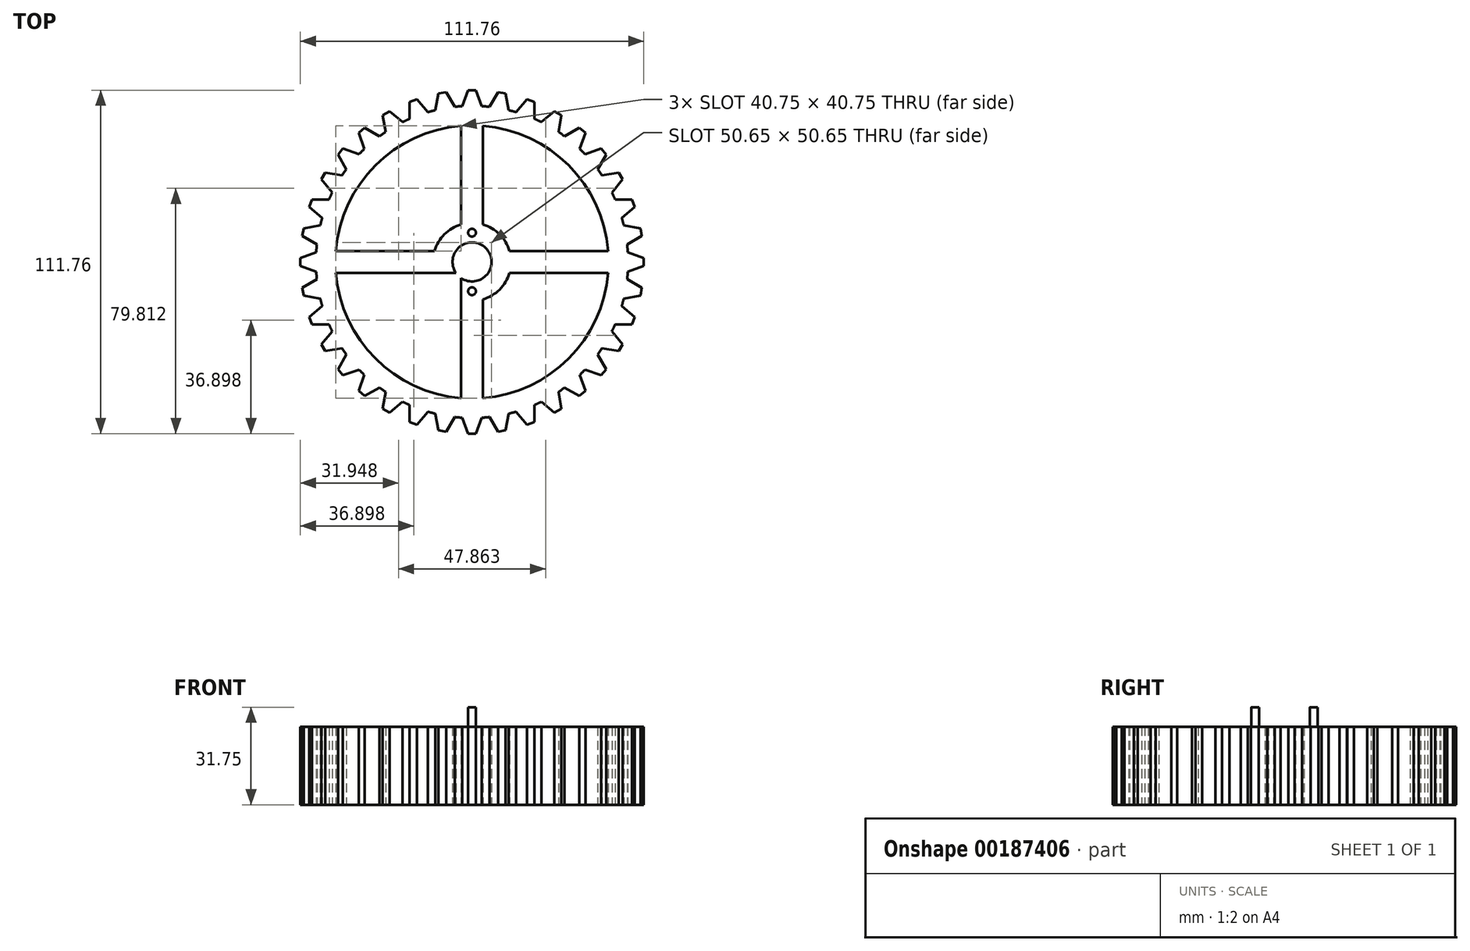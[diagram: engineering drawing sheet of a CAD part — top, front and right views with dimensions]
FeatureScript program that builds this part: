
annotation { "Feature Type Name" : "Feature", "Feature Type Description" : "" }
export const myFeature = defineFeature(function(context is Context, id is Id, definition is map)
    precondition{}
    {
        {
            var Q0;
            Q0=qCreatedBy(makeId("Top.planeOp"),FACE);
            var sketch = newSketch(context, id + "F0", { "sketchPlane" : qUnion([Q0])});
            skCircle(sketch, "E0", {"center": v(0, 0) * mm, "radius": 50.8 * mm});
            skLineSegment(sketch, "E1", {"start": v(0, 49.78) * mm, "end": v(3.56, 49.78) * mm});
            skLineSegment(sketch, "E2", {"start": v(0, 49.78) * mm, "end": v(-3.56, 49.78) * mm});
            skLineSegment(sketch, "E3", {"start": v(0, 55.88) * mm, "end": v(-1.27, 55.88) * mm});
            skLineSegment(sketch, "E4", {"start": v(0, 55.88) * mm, "end": v(1.27, 55.88) * mm});
            skLineSegment(sketch, "E5", {"start": v(-1.27, 55.88) * mm, "end": v(-3.56, 49.78) * mm});
            skLineSegment(sketch, "E6", {"start": v(1.27, 55.88) * mm, "end": v(3.56, 49.78) * mm});
            skLineSegment(sketch, "E7.1.0", {"start": v(10.95, 54.81) * mm, "end": v(12.15, 48.41) * mm});
            skLineSegment(sketch, "E7.1.1", {"start": v(9.7, 55.03) * mm, "end": v(10.95, 54.81) * mm});
            skLineSegment(sketch, "E7.1.2", {"start": v(9.7, 55.03) * mm, "end": v(8.45, 55.25) * mm});
            skLineSegment(sketch, "E7.1.3", {"start": v(8.45, 55.25) * mm, "end": v(5.14, 49.65) * mm});
            skLineSegment(sketch, "E7.1.4", {"start": v(8.64, 49.03) * mm, "end": v(5.14, 49.65) * mm});
            skLineSegment(sketch, "E7.1.5", {"start": v(8.64, 49.03) * mm, "end": v(12.15, 48.41) * mm});
            skLineSegment(sketch, "E7.2.0", {"start": v(20.3, 52.08) * mm, "end": v(20.37, 45.57) * mm});
            skLineSegment(sketch, "E7.2.1", {"start": v(19.11, 52.51) * mm, "end": v(20.3, 52.08) * mm});
            skLineSegment(sketch, "E7.2.2", {"start": v(19.11, 52.51) * mm, "end": v(17.92, 52.94) * mm});
            skLineSegment(sketch, "E7.2.3", {"start": v(17.92, 52.94) * mm, "end": v(13.69, 48) * mm});
            skLineSegment(sketch, "E7.2.4", {"start": v(17.03, 46.78) * mm, "end": v(13.69, 48) * mm});
            skLineSegment(sketch, "E7.2.5", {"start": v(17.03, 46.78) * mm, "end": v(20.37, 45.57) * mm});
            skLineSegment(sketch, "E7.3.0", {"start": v(29.04, 47.76) * mm, "end": v(27.97, 41.34) * mm});
            skLineSegment(sketch, "E7.3.1", {"start": v(27.94, 48.4) * mm, "end": v(29.04, 47.76) * mm});
            skLineSegment(sketch, "E7.3.2", {"start": v(27.94, 48.4) * mm, "end": v(26.84, 49.03) * mm});
            skLineSegment(sketch, "E7.3.3", {"start": v(26.84, 49.03) * mm, "end": v(21.81, 44.9) * mm});
            skLineSegment(sketch, "E7.3.4", {"start": v(24.9, 43.11) * mm, "end": v(21.81, 44.9) * mm});
            skLineSegment(sketch, "E7.3.5", {"start": v(24.9, 43.11) * mm, "end": v(27.97, 41.34) * mm});
            skLineSegment(sketch, "E7.4.0", {"start": v(36.9, 42) * mm, "end": v(34.72, 35.85) * mm});
            skLineSegment(sketch, "E7.4.1", {"start": v(35.92, 42.8) * mm, "end": v(36.9, 42) * mm});
            skLineSegment(sketch, "E7.4.2", {"start": v(35.92, 42.8) * mm, "end": v(34.95, 43.62) * mm});
            skLineSegment(sketch, "E7.4.3", {"start": v(34.95, 43.62) * mm, "end": v(29.28, 40.42) * mm});
            skLineSegment(sketch, "E7.4.4", {"start": v(32, 38.14) * mm, "end": v(29.28, 40.42) * mm});
            skLineSegment(sketch, "E7.4.5", {"start": v(32, 38.14) * mm, "end": v(34.72, 35.85) * mm});
            skLineSegment(sketch, "E7.5.0", {"start": v(43.62, 34.95) * mm, "end": v(40.42, 29.28) * mm});
            skLineSegment(sketch, "E7.5.1", {"start": v(42.8, 35.92) * mm, "end": v(43.62, 34.95) * mm});
            skLineSegment(sketch, "E7.5.2", {"start": v(42.8, 35.92) * mm, "end": v(42, 36.9) * mm});
            skLineSegment(sketch, "E7.5.3", {"start": v(42, 36.9) * mm, "end": v(35.85, 34.72) * mm});
            skLineSegment(sketch, "E7.5.4", {"start": v(38.14, 32) * mm, "end": v(35.85, 34.72) * mm});
            skLineSegment(sketch, "E7.5.5", {"start": v(38.14, 32) * mm, "end": v(40.42, 29.28) * mm});
            skLineSegment(sketch, "E7.6.0", {"start": v(49.03, 26.84) * mm, "end": v(44.9, 21.81) * mm});
            skLineSegment(sketch, "E7.6.1", {"start": v(48.4, 27.94) * mm, "end": v(49.03, 26.84) * mm});
            skLineSegment(sketch, "E7.6.2", {"start": v(48.4, 27.94) * mm, "end": v(47.76, 29.04) * mm});
            skLineSegment(sketch, "E7.6.3", {"start": v(47.76, 29.04) * mm, "end": v(41.34, 27.97) * mm});
            skLineSegment(sketch, "E7.6.4", {"start": v(43.11, 24.9) * mm, "end": v(41.34, 27.97) * mm});
            skLineSegment(sketch, "E7.6.5", {"start": v(43.11, 24.9) * mm, "end": v(44.9, 21.81) * mm});
            skLineSegment(sketch, "E7.7.0", {"start": v(52.94, 17.92) * mm, "end": v(48, 13.69) * mm});
            skLineSegment(sketch, "E7.7.1", {"start": v(52.51, 19.11) * mm, "end": v(52.94, 17.92) * mm});
            skLineSegment(sketch, "E7.7.2", {"start": v(52.51, 19.11) * mm, "end": v(52.08, 20.3) * mm});
            skLineSegment(sketch, "E7.7.3", {"start": v(52.08, 20.3) * mm, "end": v(45.57, 20.37) * mm});
            skLineSegment(sketch, "E7.7.4", {"start": v(46.78, 17.03) * mm, "end": v(45.57, 20.37) * mm});
            skLineSegment(sketch, "E7.7.5", {"start": v(46.78, 17.03) * mm, "end": v(48, 13.69) * mm});
            skLineSegment(sketch, "E7.8.0", {"start": v(55.25, 8.45) * mm, "end": v(49.65, 5.14) * mm});
            skLineSegment(sketch, "E7.8.1", {"start": v(55.03, 9.7) * mm, "end": v(55.25, 8.45) * mm});
            skLineSegment(sketch, "E7.8.2", {"start": v(55.03, 9.7) * mm, "end": v(54.81, 10.95) * mm});
            skLineSegment(sketch, "E7.8.3", {"start": v(54.81, 10.95) * mm, "end": v(48.41, 12.15) * mm});
            skLineSegment(sketch, "E7.8.4", {"start": v(49.03, 8.64) * mm, "end": v(48.41, 12.15) * mm});
            skLineSegment(sketch, "E7.8.5", {"start": v(49.03, 8.64) * mm, "end": v(49.65, 5.14) * mm});
            skLineSegment(sketch, "E7.9.0", {"start": v(55.88, -1.27) * mm, "end": v(49.78, -3.56) * mm});
            skLineSegment(sketch, "E7.9.1", {"start": v(55.88, 0) * mm, "end": v(55.88, -1.27) * mm});
            skLineSegment(sketch, "E7.9.2", {"start": v(55.88, 0) * mm, "end": v(55.88, 1.27) * mm});
            skLineSegment(sketch, "E7.9.3", {"start": v(55.88, 1.27) * mm, "end": v(49.78, 3.56) * mm});
            skLineSegment(sketch, "E7.9.4", {"start": v(49.78, 0) * mm, "end": v(49.78, 3.56) * mm});
            skLineSegment(sketch, "E7.9.5", {"start": v(49.78, 0) * mm, "end": v(49.78, -3.56) * mm});
            skLineSegment(sketch, "E7.anchor1", {"start": v(0, 0) * mm, "end": v(3.56, 49.78) * mm, "construction": true});
            skLineSegment(sketch, "E7.anchor2", {"start": v(0, 0) * mm, "end": v(12.67, -0.9) * mm, "construction": true});
            skLineSegment(sketch, "E8.1.0", {"start": v(49.03, -8.64) * mm, "end": v(49.65, -5.14) * mm});
            skLineSegment(sketch, "E8.1.1", {"start": v(55.25, -8.45) * mm, "end": v(49.65, -5.14) * mm});
            skLineSegment(sketch, "E8.1.2", {"start": v(55.03, -9.7) * mm, "end": v(55.25, -8.45) * mm});
            skLineSegment(sketch, "E8.1.3", {"start": v(55.03, -9.7) * mm, "end": v(54.81, -10.95) * mm});
            skLineSegment(sketch, "E8.1.4", {"start": v(54.81, -10.95) * mm, "end": v(48.41, -12.15) * mm});
            skLineSegment(sketch, "E8.1.5", {"start": v(49.03, -8.64) * mm, "end": v(48.41, -12.15) * mm});
            skLineSegment(sketch, "E8.2.0", {"start": v(46.78, -17.03) * mm, "end": v(48, -13.69) * mm});
            skLineSegment(sketch, "E8.2.1", {"start": v(52.94, -17.92) * mm, "end": v(48, -13.69) * mm});
            skLineSegment(sketch, "E8.2.2", {"start": v(52.51, -19.11) * mm, "end": v(52.94, -17.92) * mm});
            skLineSegment(sketch, "E8.2.3", {"start": v(52.51, -19.11) * mm, "end": v(52.08, -20.3) * mm});
            skLineSegment(sketch, "E8.2.4", {"start": v(52.08, -20.3) * mm, "end": v(45.57, -20.37) * mm});
            skLineSegment(sketch, "E8.2.5", {"start": v(46.78, -17.03) * mm, "end": v(45.57, -20.37) * mm});
            skLineSegment(sketch, "E8.3.0", {"start": v(43.11, -24.9) * mm, "end": v(44.9, -21.81) * mm});
            skLineSegment(sketch, "E8.3.1", {"start": v(49.03, -26.84) * mm, "end": v(44.9, -21.81) * mm});
            skLineSegment(sketch, "E8.3.2", {"start": v(48.4, -27.94) * mm, "end": v(49.03, -26.84) * mm});
            skLineSegment(sketch, "E8.3.3", {"start": v(48.4, -27.94) * mm, "end": v(47.76, -29.04) * mm});
            skLineSegment(sketch, "E8.3.4", {"start": v(47.76, -29.04) * mm, "end": v(41.34, -27.97) * mm});
            skLineSegment(sketch, "E8.3.5", {"start": v(43.11, -24.9) * mm, "end": v(41.34, -27.97) * mm});
            skLineSegment(sketch, "E8.4.0", {"start": v(38.14, -32) * mm, "end": v(40.42, -29.28) * mm});
            skLineSegment(sketch, "E8.4.1", {"start": v(43.62, -34.95) * mm, "end": v(40.42, -29.28) * mm});
            skLineSegment(sketch, "E8.4.2", {"start": v(42.8, -35.92) * mm, "end": v(43.62, -34.95) * mm});
            skLineSegment(sketch, "E8.4.3", {"start": v(42.8, -35.92) * mm, "end": v(42, -36.9) * mm});
            skLineSegment(sketch, "E8.4.4", {"start": v(42, -36.9) * mm, "end": v(35.85, -34.72) * mm});
            skLineSegment(sketch, "E8.4.5", {"start": v(38.14, -32) * mm, "end": v(35.85, -34.72) * mm});
            skLineSegment(sketch, "E8.5.0", {"start": v(32, -38.14) * mm, "end": v(34.72, -35.85) * mm});
            skLineSegment(sketch, "E8.5.1", {"start": v(36.9, -42) * mm, "end": v(34.72, -35.85) * mm});
            skLineSegment(sketch, "E8.5.2", {"start": v(35.92, -42.8) * mm, "end": v(36.9, -42) * mm});
            skLineSegment(sketch, "E8.5.3", {"start": v(35.92, -42.8) * mm, "end": v(34.95, -43.62) * mm});
            skLineSegment(sketch, "E8.5.4", {"start": v(34.95, -43.62) * mm, "end": v(29.28, -40.42) * mm});
            skLineSegment(sketch, "E8.5.5", {"start": v(32, -38.14) * mm, "end": v(29.28, -40.42) * mm});
            skLineSegment(sketch, "E8.6.0", {"start": v(24.9, -43.11) * mm, "end": v(27.97, -41.34) * mm});
            skLineSegment(sketch, "E8.6.1", {"start": v(29.04, -47.76) * mm, "end": v(27.97, -41.34) * mm});
            skLineSegment(sketch, "E8.6.2", {"start": v(27.94, -48.4) * mm, "end": v(29.04, -47.76) * mm});
            skLineSegment(sketch, "E8.6.3", {"start": v(27.94, -48.4) * mm, "end": v(26.84, -49.03) * mm});
            skLineSegment(sketch, "E8.6.4", {"start": v(26.84, -49.03) * mm, "end": v(21.81, -44.9) * mm});
            skLineSegment(sketch, "E8.6.5", {"start": v(24.9, -43.11) * mm, "end": v(21.81, -44.9) * mm});
            skLineSegment(sketch, "E8.7.0", {"start": v(17.03, -46.78) * mm, "end": v(20.37, -45.57) * mm});
            skLineSegment(sketch, "E8.7.1", {"start": v(20.3, -52.08) * mm, "end": v(20.37, -45.57) * mm});
            skLineSegment(sketch, "E8.7.2", {"start": v(19.11, -52.51) * mm, "end": v(20.3, -52.08) * mm});
            skLineSegment(sketch, "E8.7.3", {"start": v(19.11, -52.51) * mm, "end": v(17.92, -52.94) * mm});
            skLineSegment(sketch, "E8.7.4", {"start": v(17.92, -52.94) * mm, "end": v(13.69, -48) * mm});
            skLineSegment(sketch, "E8.7.5", {"start": v(17.03, -46.78) * mm, "end": v(13.69, -48) * mm});
            skLineSegment(sketch, "E8.8.0", {"start": v(8.64, -49.03) * mm, "end": v(12.15, -48.41) * mm});
            skLineSegment(sketch, "E8.8.1", {"start": v(10.95, -54.81) * mm, "end": v(12.15, -48.41) * mm});
            skLineSegment(sketch, "E8.8.2", {"start": v(9.7, -55.03) * mm, "end": v(10.95, -54.81) * mm});
            skLineSegment(sketch, "E8.8.3", {"start": v(9.7, -55.03) * mm, "end": v(8.45, -55.25) * mm});
            skLineSegment(sketch, "E8.8.4", {"start": v(8.45, -55.25) * mm, "end": v(5.14, -49.65) * mm});
            skLineSegment(sketch, "E8.8.5", {"start": v(8.64, -49.03) * mm, "end": v(5.14, -49.65) * mm});
            skLineSegment(sketch, "E8.9.0", {"start": v(0, -49.78) * mm, "end": v(3.56, -49.78) * mm});
            skLineSegment(sketch, "E8.9.1", {"start": v(1.27, -55.88) * mm, "end": v(3.56, -49.78) * mm});
            skLineSegment(sketch, "E8.9.2", {"start": v(0, -55.88) * mm, "end": v(1.27, -55.88) * mm});
            skLineSegment(sketch, "E8.9.3", {"start": v(0, -55.88) * mm, "end": v(-1.27, -55.88) * mm});
            skLineSegment(sketch, "E8.9.4", {"start": v(-1.27, -55.88) * mm, "end": v(-3.56, -49.78) * mm});
            skLineSegment(sketch, "E8.9.5", {"start": v(0, -49.78) * mm, "end": v(-3.56, -49.78) * mm});
            skLineSegment(sketch, "E8.anchor1", {"start": v(0, 0) * mm, "end": v(12.7, 0) * mm, "construction": true});
            skLineSegment(sketch, "E8.anchor2", {"start": v(0, 0) * mm, "end": v(0, -49.78) * mm, "construction": true});
            skLineSegment(sketch, "E9.MirrorCS", {"start": v(-42.8, -35.92) * mm, "end": v(-42, -36.9) * mm});
            skLineSegment(sketch, "E10.MirrorCS", {"start": v(-42.8, -35.92) * mm, "end": v(-43.62, -34.95) * mm});
            skLineSegment(sketch, "E11.MirrorCS", {"start": v(-24.9, -43.11) * mm, "end": v(-21.81, -44.9) * mm});
            skLineSegment(sketch, "E12.MirrorCS", {"start": v(-8.64, 49.03) * mm, "end": v(-5.14, 49.65) * mm});
            skLineSegment(sketch, "E13.MirrorCS", {"start": v(-8.45, 55.25) * mm, "end": v(-5.14, 49.65) * mm});
            skLineSegment(sketch, "E14.MirrorCS", {"start": v(-9.7, 55.03) * mm, "end": v(-8.45, 55.25) * mm});
            skLineSegment(sketch, "E15.MirrorCS", {"start": v(-9.7, 55.03) * mm, "end": v(-10.95, 54.81) * mm});
            skLineSegment(sketch, "E16.MirrorCS", {"start": v(-9.7, -55.03) * mm, "end": v(-8.45, -55.25) * mm});
            skLineSegment(sketch, "E17.MirrorCS", {"start": v(-49.78, 0) * mm, "end": v(-49.78, -3.56) * mm});
            skLineSegment(sketch, "E18.MirrorCS", {"start": v(-8.45, -55.25) * mm, "end": v(-5.14, -49.65) * mm});
            skLineSegment(sketch, "E19.MirrorCS", {"start": v(-55.88, 0) * mm, "end": v(-55.88, 1.27) * mm});
            skLineSegment(sketch, "E20.MirrorCS", {"start": v(-55.88, 0) * mm, "end": v(-55.88, -1.27) * mm});
            skLineSegment(sketch, "E21.MirrorCS", {"start": v(-48.4, -27.94) * mm, "end": v(-49.03, -26.84) * mm});
            skLineSegment(sketch, "E22.MirrorCS", {"start": v(-49.78, 0) * mm, "end": v(-49.78, 3.56) * mm});
            skLineSegment(sketch, "E23.MirrorCS", {"start": v(-9.7, -55.03) * mm, "end": v(-10.95, -54.81) * mm});
            skLineSegment(sketch, "E24.MirrorCS", {"start": v(-55.88, -1.27) * mm, "end": v(-49.78, -3.56) * mm});
            skLineSegment(sketch, "E25.MirrorCS", {"start": v(-55.88, 1.27) * mm, "end": v(-49.78, 3.56) * mm});
            skLineSegment(sketch, "E26.MirrorCS", {"start": v(-42, 36.9) * mm, "end": v(-35.85, 34.72) * mm});
            skLineSegment(sketch, "E27.MirrorCS", {"start": v(-55.03, 9.7) * mm, "end": v(-55.25, 8.45) * mm});
            skLineSegment(sketch, "E28.MirrorCS", {"start": v(-55.03, -9.7) * mm, "end": v(-54.81, -10.95) * mm});
            skLineSegment(sketch, "E29.MirrorCS", {"start": v(-43.62, -34.95) * mm, "end": v(-40.42, -29.28) * mm});
            skLineSegment(sketch, "E30.MirrorCS", {"start": v(-17.03, 46.78) * mm, "end": v(-20.37, 45.57) * mm});
            skLineSegment(sketch, "E31.MirrorCS", {"start": v(-26.84, -49.03) * mm, "end": v(-21.81, -44.9) * mm});
            skLineSegment(sketch, "E32.MirrorCS", {"start": v(-42.8, 35.92) * mm, "end": v(-42, 36.9) * mm});
            skLineSegment(sketch, "E33.MirrorCS", {"start": v(-55.25, 8.45) * mm, "end": v(-49.65, 5.14) * mm});
            skLineSegment(sketch, "E34.MirrorCS", {"start": v(-55.03, -9.7) * mm, "end": v(-55.25, -8.45) * mm});
            skLineSegment(sketch, "E35.MirrorCS", {"start": v(-38.14, -32) * mm, "end": v(-40.42, -29.28) * mm});
            skLineSegment(sketch, "E36.MirrorCS", {"start": v(-17.03, 46.78) * mm, "end": v(-13.69, 48) * mm});
            skLineSegment(sketch, "E37.MirrorCS", {"start": v(-42.8, 35.92) * mm, "end": v(-43.62, 34.95) * mm});
            skLineSegment(sketch, "E38.MirrorCS", {"start": v(-46.78, 17.03) * mm, "end": v(-48, 13.69) * mm});
            skLineSegment(sketch, "E39.MirrorCS", {"start": v(-55.25, -8.45) * mm, "end": v(-49.65, -5.14) * mm});
            skLineSegment(sketch, "E40.MirrorCS", {"start": v(-43.11, -24.9) * mm, "end": v(-41.34, -27.97) * mm});
            skLineSegment(sketch, "E41.MirrorCS", {"start": v(-17.92, 52.94) * mm, "end": v(-13.69, 48) * mm});
            skLineSegment(sketch, "E42.MirrorCS", {"start": v(-27.94, -48.4) * mm, "end": v(-26.84, -49.03) * mm});
            skLineSegment(sketch, "E43.MirrorCS", {"start": v(-8.64, 49.03) * mm, "end": v(-12.15, 48.41) * mm});
            skLineSegment(sketch, "E44.MirrorCS", {"start": v(-10.95, 54.81) * mm, "end": v(-12.15, 48.41) * mm});
            skLineSegment(sketch, "E45.MirrorCS", {"start": v(-19.11, 52.51) * mm, "end": v(-17.92, 52.94) * mm});
            skLineSegment(sketch, "E46.MirrorCS", {"start": v(-19.11, 52.51) * mm, "end": v(-20.3, 52.08) * mm});
            skLineSegment(sketch, "E47.MirrorCS", {"start": v(-20.3, 52.08) * mm, "end": v(-20.37, 45.57) * mm});
            skLineSegment(sketch, "E48.MirrorCS", {"start": v(-27.94, -48.4) * mm, "end": v(-29.04, -47.76) * mm});
            skLineSegment(sketch, "E49.MirrorCS", {"start": v(-43.62, 34.95) * mm, "end": v(-40.42, 29.28) * mm});
            skLineSegment(sketch, "E50.MirrorCS", {"start": v(-46.78, 17.03) * mm, "end": v(-45.57, 20.37) * mm});
            skLineSegment(sketch, "E51.MirrorCS", {"start": v(-49.03, -8.64) * mm, "end": v(-49.65, -5.14) * mm});
            skLineSegment(sketch, "E52.MirrorCS", {"start": v(-47.76, -29.04) * mm, "end": v(-41.34, -27.97) * mm});
            skLineSegment(sketch, "E53.MirrorCS", {"start": v(-29.04, -47.76) * mm, "end": v(-27.97, -41.34) * mm});
            skLineSegment(sketch, "E54.MirrorCS", {"start": v(-8.64, -49.03) * mm, "end": v(-5.14, -49.65) * mm});
            skLineSegment(sketch, "E55.MirrorCS", {"start": v(-32, 38.14) * mm, "end": v(-34.72, 35.85) * mm});
            skLineSegment(sketch, "E56.MirrorCS", {"start": v(-52.08, 20.3) * mm, "end": v(-45.57, 20.37) * mm});
            skLineSegment(sketch, "E57.MirrorCS", {"start": v(-48.4, -27.94) * mm, "end": v(-47.76, -29.04) * mm});
            skLineSegment(sketch, "E58.MirrorCS", {"start": v(-49.03, -26.84) * mm, "end": v(-44.9, -21.81) * mm});
            skLineSegment(sketch, "E59.MirrorCS", {"start": v(-32, -38.14) * mm, "end": v(-29.28, -40.42) * mm});
            skLineSegment(sketch, "E60.MirrorCS", {"start": v(-34.95, 43.62) * mm, "end": v(-29.28, 40.42) * mm});
            skLineSegment(sketch, "E61.MirrorCS", {"start": v(-52.51, 19.11) * mm, "end": v(-52.94, 17.92) * mm});
            skLineSegment(sketch, "E62.MirrorCS", {"start": v(-24.9, -43.11) * mm, "end": v(-27.97, -41.34) * mm});
            skLineSegment(sketch, "E63.MirrorCS", {"start": v(-52.51, 19.11) * mm, "end": v(-52.08, 20.3) * mm});
            skLineSegment(sketch, "E64.MirrorCS", {"start": v(-36.9, -42) * mm, "end": v(-34.72, -35.85) * mm});
            skLineSegment(sketch, "E65.MirrorCS", {"start": v(-52.94, 17.92) * mm, "end": v(-48, 13.69) * mm});
            skLineSegment(sketch, "E66.MirrorCS", {"start": v(-24.9, 43.11) * mm, "end": v(-27.97, 41.34) * mm});
            skLineSegment(sketch, "E67.MirrorCS", {"start": v(-32, 38.14) * mm, "end": v(-29.28, 40.42) * mm});
            skLineSegment(sketch, "E68.MirrorCS", {"start": v(-35.92, 42.8) * mm, "end": v(-34.95, 43.62) * mm});
            skLineSegment(sketch, "E69.MirrorCS", {"start": v(-17.03, -46.78) * mm, "end": v(-13.69, -48) * mm});
            skLineSegment(sketch, "E70.MirrorCS", {"start": v(-47.76, 29.04) * mm, "end": v(-41.34, 27.97) * mm});
            skLineSegment(sketch, "E71.MirrorCS", {"start": v(-52.51, -19.11) * mm, "end": v(-52.08, -20.3) * mm});
            skLineSegment(sketch, "E72.MirrorCS", {"start": v(-43.11, -24.9) * mm, "end": v(-44.9, -21.81) * mm});
            skLineSegment(sketch, "E73.MirrorCS", {"start": v(-34.95, -43.62) * mm, "end": v(-29.28, -40.42) * mm});
            skLineSegment(sketch, "E74.MirrorCS", {"start": v(-52.51, -19.11) * mm, "end": v(-52.94, -17.92) * mm});
            skLineSegment(sketch, "E75.MirrorCS", {"start": v(-32, -38.14) * mm, "end": v(-34.72, -35.85) * mm});
            skLineSegment(sketch, "E76.MirrorCS", {"start": v(-17.92, -52.94) * mm, "end": v(-13.69, -48) * mm});
            skLineSegment(sketch, "E77.MirrorCS", {"start": v(-24.9, 43.11) * mm, "end": v(-21.81, 44.9) * mm});
            skLineSegment(sketch, "E78.MirrorCS", {"start": v(-48.4, 27.94) * mm, "end": v(-47.76, 29.04) * mm});
            skLineSegment(sketch, "E79.MirrorCS", {"start": v(-19.11, -52.51) * mm, "end": v(-17.92, -52.94) * mm});
            skLineSegment(sketch, "E80.MirrorCS", {"start": v(-49.03, 8.64) * mm, "end": v(-49.65, 5.14) * mm});
            skLineSegment(sketch, "E81.MirrorCS", {"start": v(-48.4, 27.94) * mm, "end": v(-49.03, 26.84) * mm});
            skLineSegment(sketch, "E82.MirrorCS", {"start": v(-52.94, -17.92) * mm, "end": v(-48, -13.69) * mm});
            skLineSegment(sketch, "E83.MirrorCS", {"start": v(-38.14, -32) * mm, "end": v(-35.85, -34.72) * mm});
            skLineSegment(sketch, "E84.MirrorCS", {"start": v(-26.84, 49.03) * mm, "end": v(-21.81, 44.9) * mm});
            skLineSegment(sketch, "E85.MirrorCS", {"start": v(-19.11, -52.51) * mm, "end": v(-20.3, -52.08) * mm});
            skLineSegment(sketch, "E86.MirrorCS", {"start": v(-49.03, 8.64) * mm, "end": v(-48.41, 12.15) * mm});
            skLineSegment(sketch, "E87.MirrorCS", {"start": v(-49.03, 26.84) * mm, "end": v(-44.9, 21.81) * mm});
            skLineSegment(sketch, "E88.MirrorCS", {"start": v(-46.78, -17.03) * mm, "end": v(-48, -13.69) * mm});
            skLineSegment(sketch, "E89.MirrorCS", {"start": v(-42, -36.9) * mm, "end": v(-35.85, -34.72) * mm});
            skLineSegment(sketch, "E90.MirrorCS", {"start": v(-27.94, 48.4) * mm, "end": v(-26.84, 49.03) * mm});
            skLineSegment(sketch, "E91.MirrorCS", {"start": v(-20.3, -52.08) * mm, "end": v(-20.37, -45.57) * mm});
            skLineSegment(sketch, "E92.MirrorCS", {"start": v(-38.14, 32) * mm, "end": v(-40.42, 29.28) * mm});
            skLineSegment(sketch, "E93.MirrorCS", {"start": v(-54.81, 10.95) * mm, "end": v(-48.41, 12.15) * mm});
            skLineSegment(sketch, "E94.MirrorCS", {"start": v(-49.03, -8.64) * mm, "end": v(-48.41, -12.15) * mm});
            skLineSegment(sketch, "E95.MirrorCS", {"start": v(-27.94, 48.4) * mm, "end": v(-29.04, 47.76) * mm});
            skLineSegment(sketch, "E96.MirrorCS", {"start": v(-46.78, -17.03) * mm, "end": v(-45.57, -20.37) * mm});
            skLineSegment(sketch, "E97.MirrorCS", {"start": v(-35.92, 42.8) * mm, "end": v(-36.9, 42) * mm});
            skLineSegment(sketch, "E98.MirrorCS", {"start": v(-35.92, -42.8) * mm, "end": v(-34.95, -43.62) * mm});
            skLineSegment(sketch, "E99.MirrorCS", {"start": v(-10.95, -54.81) * mm, "end": v(-12.15, -48.41) * mm});
            skLineSegment(sketch, "E100.MirrorCS", {"start": v(-43.11, 24.9) * mm, "end": v(-44.9, 21.81) * mm});
            skLineSegment(sketch, "E101.MirrorCS", {"start": v(-17.03, -46.78) * mm, "end": v(-20.37, -45.57) * mm});
            skLineSegment(sketch, "E102.MirrorCS", {"start": v(-38.14, 32) * mm, "end": v(-35.85, 34.72) * mm});
            skLineSegment(sketch, "E103.MirrorCS", {"start": v(-55.03, 9.7) * mm, "end": v(-54.81, 10.95) * mm});
            skLineSegment(sketch, "E104.MirrorCS", {"start": v(-54.81, -10.95) * mm, "end": v(-48.41, -12.15) * mm});
            skLineSegment(sketch, "E105.MirrorCS", {"start": v(-29.04, 47.76) * mm, "end": v(-27.97, 41.34) * mm});
            skLineSegment(sketch, "E106.MirrorCS", {"start": v(-43.11, 24.9) * mm, "end": v(-41.34, 27.97) * mm});
            skLineSegment(sketch, "E107.MirrorCS", {"start": v(-35.92, -42.8) * mm, "end": v(-36.9, -42) * mm});
            skLineSegment(sketch, "E108.MirrorCS", {"start": v(-52.08, -20.3) * mm, "end": v(-45.57, -20.37) * mm});
            skLineSegment(sketch, "E109.MirrorCS", {"start": v(-8.64, -49.03) * mm, "end": v(-12.15, -48.41) * mm});
            skLineSegment(sketch, "E110.MirrorCS", {"start": v(-36.9, 42) * mm, "end": v(-34.72, 35.85) * mm});
            skLineSegment(sketch, "E111.MirrorCS", {"start": v(0, 0) * mm, "end": v(-6.33, -0.45) * mm, "construction": true});
            skLineSegment(sketch, "E112.MirrorCS", {"start": v(0, 0) * mm, "end": v(-3.56, 49.78) * mm, "construction": true});
            skLineSegment(sketch, "E113.MirrorCS", {"start": v(0, 0) * mm, "end": v(-12.7, 0) * mm, "construction": true});
            skCircle(sketch, "E114", {"center": v(0, 0) * mm, "radius": 44.45 * mm});
            skCircle(sketch, "E115", {"center": v(0, 0) * mm, "radius": 6.35 * mm});
            skCircle(sketch, "E116", {"center": v(0, 0) * mm, "radius": 12.7 * mm});
            skLineSegment(sketch, "E117", {"start": v(0, 0) * mm, "end": v(0, 55.88) * mm});
            skLineSegment(sketch, "E118", {"start": v(0, 0) * mm, "end": v(0, -55.88) * mm});
            skLineSegment(sketch, "E119", {"start": v(0, 0) * mm, "end": v(55.88, 0) * mm});
            skLineSegment(sketch, "E120", {"start": v(0, 0) * mm, "end": v(-55.88, 0) * mm});
            skLineSegment(sketch, "E121.bottom", {"start": v(-49.78, 3.56) * mm, "end": v(49.78, 3.56) * mm});
            skLineSegment(sketch, "E121.top", {"start": v(-49.78, -3.56) * mm, "end": v(49.78, -3.56) * mm});
            skLineSegment(sketch, "E121.left", {"start": v(-49.78, 3.56) * mm, "end": v(-49.78, -3.56) * mm});
            skLineSegment(sketch, "E121.right", {"start": v(49.78, 3.56) * mm, "end": v(49.78, -3.56) * mm});
            skLineSegment(sketch, "E122.bottom", {"start": v(-3.56, 49.78) * mm, "end": v(3.56, 49.78) * mm});
            skLineSegment(sketch, "E122.top", {"start": v(-3.56, -49.78) * mm, "end": v(3.56, -49.78) * mm});
            skLineSegment(sketch, "E122.left", {"start": v(-3.56, 49.78) * mm, "end": v(-3.56, -49.78) * mm});
            skLineSegment(sketch, "E122.right", {"start": v(3.56, 49.78) * mm, "end": v(3.56, -49.78) * mm});
            skLineSegment(sketch, "E123.trimOffspring", {"start": v(-44.45, 0) * mm, "end": v(-49.78, 0) * mm, "construction": true});
            skLineSegment(sketch, "E124.trimOffspring", {"start": v(44.34, -3.17) * mm, "end": v(49.78, -3.56) * mm, "construction": true});
            skLineSegment(sketch, "E125.trimOffspring", {"start": v(44.45, 0) * mm, "end": v(49.78, 0) * mm, "construction": true});
            skLineSegment(sketch, "E126.trimOffspring", {"start": v(-44.34, -3.17) * mm, "end": v(-49.78, -3.56) * mm, "construction": true});
            skSolve(sketch);
        }
        {
            var Q0;
            Q0 = qSketchRegion(id + "F0", true);
            var Q1;
            {var subQ0=sQuery(id+"F0.wireOp",EDGE,"E117");var subQ1=sQuery(id+"F0.wireOp",EDGE,"E114");var subQ2=makeQuery(id+"F0.imprint","INTERSECT",VERTEX,{"derivedFrom":[subQ1,subQ0]});Q1=makeQuery(id+"F0.imprint","IMPRINT",FACE,{"disambiguationData":[TD([[makeQuery(id+"F0.imprint","IMPRINT",EDGE,{"disambiguationData":[TD([[subQ2,-1.0]])],"derivedFrom":subQ1}),-1.0]])]});}
            var Q2;
            {var subQ0=sQuery(id+"F0.wireOp",EDGE,"E122.right");var subQ1=sQuery(id+"F0.wireOp",EDGE,"E114");var subQ2=makeQuery(id+"F0.imprint","INTERSECT",VERTEX,{"disambiguationData":[OD(0.0)],"derivedFrom":[subQ1,subQ0]});Q2=makeQuery(id+"F0.imprint","IMPRINT",FACE,{"disambiguationData":[TD([[makeQuery(id+"F0.imprint","IMPRINT",EDGE,{"disambiguationData":[TD([[subQ2,-1.0]])],"derivedFrom":subQ1}),-1.0]])]});}
            var Q3;
            {var subQ0=sQuery(id+"F0.wireOp",EDGE,"E121.bottom");var subQ1=sQuery(id+"F0.wireOp",EDGE,"E114");var subQ2=makeQuery(id+"F0.imprint","INTERSECT",VERTEX,{"disambiguationData":[OD(1.0)],"derivedFrom":[subQ1,subQ0]});Q3=makeQuery(id+"F0.imprint","IMPRINT",FACE,{"disambiguationData":[TD([[makeQuery(id+"F0.imprint","IMPRINT",EDGE,{"disambiguationData":[TD([[subQ2,-1.0]])],"derivedFrom":subQ1}),-1.0]])]});}
            var Q4;
            {var subQ0=sQuery(id+"F0.wireOp",EDGE,"E120");var subQ1=sQuery(id+"F0.wireOp",EDGE,"E114");var subQ2=makeQuery(id+"F0.imprint","INTERSECT",VERTEX,{"derivedFrom":[subQ1,subQ0]});Q4=makeQuery(id+"F0.imprint","IMPRINT",FACE,{"disambiguationData":[TD([[makeQuery(id+"F0.imprint","IMPRINT",EDGE,{"disambiguationData":[TD([[subQ2,-1.0]])],"derivedFrom":subQ1}),-1.0]])]});}
            var Q5;
            {var subQ0=sQuery(id+"F0.wireOp",EDGE,"E121.bottom");var subQ1=sQuery(id+"F0.wireOp",EDGE,"E114");var subQ2=makeQuery(id+"F0.imprint","INTERSECT",VERTEX,{"disambiguationData":[OD(0.0)],"derivedFrom":[subQ1,subQ0]});Q5=makeQuery(id+"F0.imprint","IMPRINT",FACE,{"disambiguationData":[TD([[makeQuery(id+"F0.imprint","IMPRINT",EDGE,{"disambiguationData":[TD([[subQ2,1.0]])],"derivedFrom":subQ1}),-1.0]])]});}
            var Q6;
            {var subQ0=sQuery(id+"F0.wireOp",EDGE,"E119");var subQ1=sQuery(id+"F0.wireOp",EDGE,"E114");var subQ2=makeQuery(id+"F0.imprint","INTERSECT",VERTEX,{"derivedFrom":[subQ1,subQ0]});Q6=makeQuery(id+"F0.imprint","IMPRINT",FACE,{"disambiguationData":[TD([[makeQuery(id+"F0.imprint","IMPRINT",EDGE,{"disambiguationData":[TD([[subQ2,1.0]])],"derivedFrom":subQ1}),-1.0]])]});}
            var Q7;
            {var subQ0=sQuery(id+"F0.wireOp",EDGE,"E118");var subQ1=sQuery(id+"F0.wireOp",EDGE,"E114");var subQ2=makeQuery(id+"F0.imprint","INTERSECT",VERTEX,{"derivedFrom":[subQ1,subQ0]});Q7=makeQuery(id+"F0.imprint","IMPRINT",FACE,{"disambiguationData":[TD([[makeQuery(id+"F0.imprint","IMPRINT",EDGE,{"disambiguationData":[TD([[subQ2,-1.0]])],"derivedFrom":subQ1}),-1.0]])]});}
            var Q8;
            {var subQ0=sQuery(id+"F0.wireOp",EDGE,"E122.left");var subQ1=sQuery(id+"F0.wireOp",EDGE,"E114");var subQ2=makeQuery(id+"F0.imprint","INTERSECT",VERTEX,{"disambiguationData":[OD(1.0)],"derivedFrom":[subQ1,subQ0]});Q8=makeQuery(id+"F0.imprint","IMPRINT",FACE,{"disambiguationData":[TD([[makeQuery(id+"F0.imprint","IMPRINT",EDGE,{"disambiguationData":[TD([[subQ2,-1.0]])],"derivedFrom":subQ1}),-1.0]])]});}
            var Q9;
            {var subQ0=sQuery(id+"F0.wireOp",EDGE,"E118");var subQ1=sQuery(id+"F0.wireOp",EDGE,"E115");var subQ2=makeQuery(id+"F0.imprint","INTERSECT",VERTEX,{"derivedFrom":[subQ1,subQ0]});Q9=makeQuery(id+"F0.imprint","IMPRINT",FACE,{"disambiguationData":[TD([[makeQuery(id+"F0.imprint","IMPRINT",EDGE,{"disambiguationData":[TD([[subQ2,-1.0]])],"derivedFrom":subQ1}),-1.0]])]});}
            var Q10;
            {var subQ0=sQuery(id+"F0.wireOp",EDGE,"E122.left");var subQ1=sQuery(id+"F0.wireOp",EDGE,"E115");var subQ2=makeQuery(id+"F0.imprint","INTERSECT",VERTEX,{"disambiguationData":[OD(1.0)],"derivedFrom":[subQ1,subQ0]});Q10=makeQuery(id+"F0.imprint","IMPRINT",FACE,{"disambiguationData":[TD([[makeQuery(id+"F0.imprint","IMPRINT",EDGE,{"disambiguationData":[TD([[subQ2,-1.0]])],"derivedFrom":subQ1}),-1.0]])]});}
            var Q11;
            {var subQ0=sQuery(id+"F0.wireOp",EDGE,"E121.top");var subQ1=sQuery(id+"F0.wireOp",EDGE,"E115");var subQ2=makeQuery(id+"F0.imprint","INTERSECT",VERTEX,{"disambiguationData":[OD(0.0)],"derivedFrom":[subQ1,subQ0]});Q11=makeQuery(id+"F0.imprint","IMPRINT",FACE,{"disambiguationData":[TD([[makeQuery(id+"F0.imprint","IMPRINT",EDGE,{"disambiguationData":[TD([[subQ2,-1.0]])],"derivedFrom":subQ1}),-1.0]])]});}
            var Q12;
            {var subQ0=sQuery(id+"F0.wireOp",EDGE,"E120");var subQ1=sQuery(id+"F0.wireOp",EDGE,"E115");var subQ2=makeQuery(id+"F0.imprint","INTERSECT",VERTEX,{"derivedFrom":[subQ1,subQ0]});Q12=makeQuery(id+"F0.imprint","IMPRINT",FACE,{"disambiguationData":[TD([[makeQuery(id+"F0.imprint","IMPRINT",EDGE,{"disambiguationData":[TD([[subQ2,-1.0]])],"derivedFrom":subQ1}),-1.0]])]});}
            var Q13;
            {var subQ0=sQuery(id+"F0.wireOp",EDGE,"E121.bottom");var subQ1=sQuery(id+"F0.wireOp",EDGE,"E115");var subQ2=makeQuery(id+"F0.imprint","INTERSECT",VERTEX,{"disambiguationData":[OD(1.0)],"derivedFrom":[subQ1,subQ0]});Q13=makeQuery(id+"F0.imprint","IMPRINT",FACE,{"disambiguationData":[TD([[makeQuery(id+"F0.imprint","IMPRINT",EDGE,{"disambiguationData":[TD([[subQ2,-1.0]])],"derivedFrom":subQ1}),-1.0]])]});}
            var Q14;
            {var subQ0=sQuery(id+"F0.wireOp",EDGE,"E122.left");var subQ1=sQuery(id+"F0.wireOp",EDGE,"E115");var subQ2=makeQuery(id+"F0.imprint","INTERSECT",VERTEX,{"disambiguationData":[OD(0.0)],"derivedFrom":[subQ1,subQ0]});Q14=makeQuery(id+"F0.imprint","IMPRINT",FACE,{"disambiguationData":[TD([[makeQuery(id+"F0.imprint","IMPRINT",EDGE,{"disambiguationData":[TD([[subQ2,-1.0]])],"derivedFrom":subQ1}),-1.0]])]});}
            var Q15;
            {var subQ0=sQuery(id+"F0.wireOp",EDGE,"E117");var subQ1=sQuery(id+"F0.wireOp",EDGE,"E115");var subQ2=makeQuery(id+"F0.imprint","INTERSECT",VERTEX,{"derivedFrom":[subQ1,subQ0]});Q15=makeQuery(id+"F0.imprint","IMPRINT",FACE,{"disambiguationData":[TD([[makeQuery(id+"F0.imprint","IMPRINT",EDGE,{"disambiguationData":[TD([[subQ2,-1.0]])],"derivedFrom":subQ1}),-1.0]])]});}
            var Q16;
            {var subQ0=sQuery(id+"F0.wireOp",EDGE,"E122.right");var subQ1=sQuery(id+"F0.wireOp",EDGE,"E115");var subQ2=makeQuery(id+"F0.imprint","INTERSECT",VERTEX,{"disambiguationData":[OD(0.0)],"derivedFrom":[subQ1,subQ0]});Q16=makeQuery(id+"F0.imprint","IMPRINT",FACE,{"disambiguationData":[TD([[makeQuery(id+"F0.imprint","IMPRINT",EDGE,{"disambiguationData":[TD([[subQ2,-1.0]])],"derivedFrom":subQ1}),-1.0]])]});}
            var Q17;
            {var subQ0=sQuery(id+"F0.wireOp",EDGE,"E121.bottom");var subQ1=sQuery(id+"F0.wireOp",EDGE,"E115");var subQ2=makeQuery(id+"F0.imprint","INTERSECT",VERTEX,{"disambiguationData":[OD(0.0)],"derivedFrom":[subQ1,subQ0]});Q17=makeQuery(id+"F0.imprint","IMPRINT",FACE,{"disambiguationData":[TD([[makeQuery(id+"F0.imprint","IMPRINT",EDGE,{"disambiguationData":[TD([[subQ2,-1.0]])],"derivedFrom":subQ1}),-1.0]])]});}
            var Q18;
            {var subQ0=sQuery(id+"F0.wireOp",EDGE,"E121.bottom");var subQ1=sQuery(id+"F0.wireOp",EDGE,"E115");var subQ2=makeQuery(id+"F0.imprint","INTERSECT",VERTEX,{"disambiguationData":[OD(0.0)],"derivedFrom":[subQ1,subQ0]});Q18=makeQuery(id+"F0.imprint","IMPRINT",FACE,{"disambiguationData":[TD([[makeQuery(id+"F0.imprint","IMPRINT",EDGE,{"disambiguationData":[TD([[subQ2,1.0]])],"derivedFrom":subQ1}),-1.0]])]});}
            var Q19;
            {var subQ0=sQuery(id+"F0.wireOp",EDGE,"E119");var subQ1=sQuery(id+"F0.wireOp",EDGE,"E115");var subQ2=makeQuery(id+"F0.imprint","INTERSECT",VERTEX,{"derivedFrom":[subQ1,subQ0]});Q19=makeQuery(id+"F0.imprint","IMPRINT",FACE,{"disambiguationData":[TD([[makeQuery(id+"F0.imprint","IMPRINT",EDGE,{"disambiguationData":[TD([[subQ2,1.0]])],"derivedFrom":subQ1}),-1.0]])]});}
            var Q20;
            {var subQ0=sQuery(id+"F0.wireOp",EDGE,"E122.right");var subQ1=sQuery(id+"F0.wireOp",EDGE,"E115");var subQ2=makeQuery(id+"F0.imprint","INTERSECT",VERTEX,{"disambiguationData":[OD(1.0)],"derivedFrom":[subQ1,subQ0]});Q20=makeQuery(id+"F0.imprint","IMPRINT",FACE,{"disambiguationData":[TD([[makeQuery(id+"F0.imprint","IMPRINT",EDGE,{"disambiguationData":[TD([[subQ2,-1.0]])],"derivedFrom":subQ1}),-1.0]])]});}
            var Q21;
            {var subQ0=sQuery(id+"F0.wireOp",EDGE,"E121.bottom");var subQ1=sQuery(id+"F0.wireOp",EDGE,"E114");var subQ2=makeQuery(id+"F0.imprint","INTERSECT",VERTEX,{"disambiguationData":[OD(1.0)],"derivedFrom":[subQ1,subQ0]});Q21=makeQuery(id+"F0.imprint","IMPRINT",FACE,{"disambiguationData":[TD([[makeQuery(id+"F0.imprint","IMPRINT",EDGE,{"disambiguationData":[TD([[subQ2,-1.0]])],"derivedFrom":subQ1}),1.0]])]});}
            var Q22;
            {var subQ0=sQuery(id+"F0.wireOp",EDGE,"E120");var subQ1=sQuery(id+"F0.wireOp",EDGE,"E114");var subQ2=makeQuery(id+"F0.imprint","INTERSECT",VERTEX,{"derivedFrom":[subQ1,subQ0]});Q22=makeQuery(id+"F0.imprint","IMPRINT",FACE,{"disambiguationData":[TD([[makeQuery(id+"F0.imprint","IMPRINT",EDGE,{"disambiguationData":[TD([[subQ2,-1.0]])],"derivedFrom":subQ1}),1.0]])]});}
            var Q23;
            {var subQ0=sQuery(id+"F0.wireOp",EDGE,"E122.left");var subQ1=sQuery(id+"F0.wireOp",EDGE,"E114");var subQ2=makeQuery(id+"F0.imprint","INTERSECT",VERTEX,{"disambiguationData":[OD(1.0)],"derivedFrom":[subQ1,subQ0]});Q23=makeQuery(id+"F0.imprint","IMPRINT",FACE,{"disambiguationData":[TD([[makeQuery(id+"F0.imprint","IMPRINT",EDGE,{"disambiguationData":[TD([[subQ2,-1.0]])],"derivedFrom":subQ1}),1.0]])]});}
            var Q24;
            {var subQ0=sQuery(id+"F0.wireOp",EDGE,"E118");var subQ1=sQuery(id+"F0.wireOp",EDGE,"E114");var subQ2=makeQuery(id+"F0.imprint","INTERSECT",VERTEX,{"derivedFrom":[subQ1,subQ0]});Q24=makeQuery(id+"F0.imprint","IMPRINT",FACE,{"disambiguationData":[TD([[makeQuery(id+"F0.imprint","IMPRINT",EDGE,{"disambiguationData":[TD([[subQ2,-1.0]])],"derivedFrom":subQ1}),1.0]])]});}
            var Q25;
            {var subQ0=sQuery(id+"F0.wireOp",EDGE,"E119");var subQ1=sQuery(id+"F0.wireOp",EDGE,"E114");var subQ2=makeQuery(id+"F0.imprint","INTERSECT",VERTEX,{"derivedFrom":[subQ1,subQ0]});Q25=makeQuery(id+"F0.imprint","IMPRINT",FACE,{"disambiguationData":[TD([[makeQuery(id+"F0.imprint","IMPRINT",EDGE,{"disambiguationData":[TD([[subQ2,1.0]])],"derivedFrom":subQ1}),1.0]])]});}
            var Q26;
            {var subQ0=sQuery(id+"F0.wireOp",EDGE,"E121.bottom");var subQ1=sQuery(id+"F0.wireOp",EDGE,"E114");var subQ2=makeQuery(id+"F0.imprint","INTERSECT",VERTEX,{"disambiguationData":[OD(0.0)],"derivedFrom":[subQ1,subQ0]});Q26=makeQuery(id+"F0.imprint","IMPRINT",FACE,{"disambiguationData":[TD([[makeQuery(id+"F0.imprint","IMPRINT",EDGE,{"disambiguationData":[TD([[subQ2,1.0]])],"derivedFrom":subQ1}),1.0]])]});}
            var Q27;
            {var subQ0=sQuery(id+"F0.wireOp",EDGE,"E122.right");var subQ1=sQuery(id+"F0.wireOp",EDGE,"E114");var subQ2=makeQuery(id+"F0.imprint","INTERSECT",VERTEX,{"disambiguationData":[OD(0.0)],"derivedFrom":[subQ1,subQ0]});Q27=makeQuery(id+"F0.imprint","IMPRINT",FACE,{"disambiguationData":[TD([[makeQuery(id+"F0.imprint","IMPRINT",EDGE,{"disambiguationData":[TD([[subQ2,-1.0]])],"derivedFrom":subQ1}),1.0]])]});}
            var Q28;
            {var subQ0=sQuery(id+"F0.wireOp",EDGE,"E117");var subQ1=sQuery(id+"F0.wireOp",EDGE,"E114");var subQ2=makeQuery(id+"F0.imprint","INTERSECT",VERTEX,{"derivedFrom":[subQ1,subQ0]});Q28=makeQuery(id+"F0.imprint","IMPRINT",FACE,{"disambiguationData":[TD([[makeQuery(id+"F0.imprint","IMPRINT",EDGE,{"disambiguationData":[TD([[subQ2,-1.0]])],"derivedFrom":subQ1}),1.0]])]});}
            extrude(context, id + "F1", {"entities" : qUnion([Q0, Q1, Q2, Q3, Q4, Q5, Q6, Q7, Q8, Q9, Q10, Q11, Q12, Q13, Q14, Q15, Q16, Q17, Q18, Q19, Q20, Q21, Q22, Q23, Q24, Q25, Q26, Q27, Q28]), "depth" : 25.4 * mm});
        }
        {
            var Q0;
            Q0=makeQuery(id+"F1.opExtrude","CAP_FACE",FACE,{"disambiguationData":[OSD([sQuery(id+"F0.wireOp",EDGE,"E0"),sQuery(id+"F0.wireOp",EDGE,"E7.1.0"),sQuery(id+"F0.wireOp",EDGE,"E7.1.1"),sQuery(id+"F0.wireOp",EDGE,"E7.1.2"),sQuery(id+"F0.wireOp",EDGE,"E7.1.3"),sQuery(id+"F0.wireOp",EDGE,"E7.2.0"),sQuery(id+"F0.wireOp",EDGE,"E7.2.1"),sQuery(id+"F0.wireOp",EDGE,"E7.2.2"),sQuery(id+"F0.wireOp",EDGE,"E7.2.3"),sQuery(id+"F0.wireOp",EDGE,"E7.3.0"),sQuery(id+"F0.wireOp",EDGE,"E7.3.1"),sQuery(id+"F0.wireOp",EDGE,"E7.3.2"),sQuery(id+"F0.wireOp",EDGE,"E7.3.3"),sQuery(id+"F0.wireOp",EDGE,"E7.4.0"),sQuery(id+"F0.wireOp",EDGE,"E7.4.1"),sQuery(id+"F0.wireOp",EDGE,"E7.4.2"),sQuery(id+"F0.wireOp",EDGE,"E7.4.3"),sQuery(id+"F0.wireOp",EDGE,"E7.5.0"),sQuery(id+"F0.wireOp",EDGE,"E7.5.1"),sQuery(id+"F0.wireOp",EDGE,"E7.5.2"),sQuery(id+"F0.wireOp",EDGE,"E7.5.3"),sQuery(id+"F0.wireOp",EDGE,"E7.6.0"),sQuery(id+"F0.wireOp",EDGE,"E7.6.1"),sQuery(id+"F0.wireOp",EDGE,"E7.6.2"),sQuery(id+"F0.wireOp",EDGE,"E7.6.3"),sQuery(id+"F0.wireOp",EDGE,"E7.7.0"),sQuery(id+"F0.wireOp",EDGE,"E7.7.1"),sQuery(id+"F0.wireOp",EDGE,"E7.7.2"),sQuery(id+"F0.wireOp",EDGE,"E7.7.3"),sQuery(id+"F0.wireOp",EDGE,"E7.8.0"),sQuery(id+"F0.wireOp",EDGE,"E7.8.1"),sQuery(id+"F0.wireOp",EDGE,"E7.8.2"),sQuery(id+"F0.wireOp",EDGE,"E7.8.3"),sQuery(id+"F0.wireOp",EDGE,"E7.9.0"),sQuery(id+"F0.wireOp",EDGE,"E7.9.1"),sQuery(id+"F0.wireOp",EDGE,"E7.9.2"),sQuery(id+"F0.wireOp",EDGE,"E7.9.3"),sQuery(id+"F0.wireOp",EDGE,"E8.1.1"),sQuery(id+"F0.wireOp",EDGE,"E8.1.2"),sQuery(id+"F0.wireOp",EDGE,"E8.1.3"),sQuery(id+"F0.wireOp",EDGE,"E8.1.4"),sQuery(id+"F0.wireOp",EDGE,"E8.2.1"),sQuery(id+"F0.wireOp",EDGE,"E8.2.2"),sQuery(id+"F0.wireOp",EDGE,"E8.2.3"),sQuery(id+"F0.wireOp",EDGE,"E8.2.4"),sQuery(id+"F0.wireOp",EDGE,"E8.3.1"),sQuery(id+"F0.wireOp",EDGE,"E8.3.2"),sQuery(id+"F0.wireOp",EDGE,"E8.3.3"),sQuery(id+"F0.wireOp",EDGE,"E8.3.4"),sQuery(id+"F0.wireOp",EDGE,"E8.4.1"),sQuery(id+"F0.wireOp",EDGE,"E8.4.2"),sQuery(id+"F0.wireOp",EDGE,"E8.4.3"),sQuery(id+"F0.wireOp",EDGE,"E8.4.4"),sQuery(id+"F0.wireOp",EDGE,"E8.5.1"),sQuery(id+"F0.wireOp",EDGE,"E8.5.2"),sQuery(id+"F0.wireOp",EDGE,"E8.5.3"),sQuery(id+"F0.wireOp",EDGE,"E8.5.4"),sQuery(id+"F0.wireOp",EDGE,"E8.6.1"),sQuery(id+"F0.wireOp",EDGE,"E8.6.2"),sQuery(id+"F0.wireOp",EDGE,"E8.6.3"),sQuery(id+"F0.wireOp",EDGE,"E8.6.4"),sQuery(id+"F0.wireOp",EDGE,"E8.7.1"),sQuery(id+"F0.wireOp",EDGE,"E8.7.2"),sQuery(id+"F0.wireOp",EDGE,"E8.7.3"),sQuery(id+"F0.wireOp",EDGE,"E8.7.4"),sQuery(id+"F0.wireOp",EDGE,"E8.8.1"),sQuery(id+"F0.wireOp",EDGE,"E8.8.2"),sQuery(id+"F0.wireOp",EDGE,"E8.8.3"),sQuery(id+"F0.wireOp",EDGE,"E8.8.4"),sQuery(id+"F0.wireOp",EDGE,"E9.MirrorCS"),sQuery(id+"F0.wireOp",EDGE,"E10.MirrorCS"),sQuery(id+"F0.wireOp",EDGE,"E13.MirrorCS"),sQuery(id+"F0.wireOp",EDGE,"E14.MirrorCS"),sQuery(id+"F0.wireOp",EDGE,"E15.MirrorCS"),sQuery(id+"F0.wireOp",EDGE,"E5"),sQuery(id+"F0.wireOp",EDGE,"E3"),sQuery(id+"F0.wireOp",EDGE,"E4"),sQuery(id+"F0.wireOp",EDGE,"E16.MirrorCS"),sQuery(id+"F0.wireOp",EDGE,"E18.MirrorCS"),sQuery(id+"F0.wireOp",EDGE,"E19.MirrorCS"),sQuery(id+"F0.wireOp",EDGE,"E20.MirrorCS"),sQuery(id+"F0.wireOp",EDGE,"E21.MirrorCS"),sQuery(id+"F0.wireOp",EDGE,"E23.MirrorCS"),sQuery(id+"F0.wireOp",EDGE,"E24.MirrorCS"),sQuery(id+"F0.wireOp",EDGE,"E25.MirrorCS"),sQuery(id+"F0.wireOp",EDGE,"E8.9.2"),sQuery(id+"F0.wireOp",EDGE,"E26.MirrorCS"),sQuery(id+"F0.wireOp",EDGE,"E27.MirrorCS"),sQuery(id+"F0.wireOp",EDGE,"E28.MirrorCS"),sQuery(id+"F0.wireOp",EDGE,"E29.MirrorCS"),sQuery(id+"F0.wireOp",EDGE,"E31.MirrorCS"),sQuery(id+"F0.wireOp",EDGE,"E8.9.3"),sQuery(id+"F0.wireOp",EDGE,"E32.MirrorCS"),sQuery(id+"F0.wireOp",EDGE,"E33.MirrorCS"),sQuery(id+"F0.wireOp",EDGE,"E34.MirrorCS"),sQuery(id+"F0.wireOp",EDGE,"E37.MirrorCS"),sQuery(id+"F0.wireOp",EDGE,"E39.MirrorCS"),sQuery(id+"F0.wireOp",EDGE,"E41.MirrorCS"),sQuery(id+"F0.wireOp",EDGE,"E42.MirrorCS"),sQuery(id+"F0.wireOp",EDGE,"E8.9.4"),sQuery(id+"F0.wireOp",EDGE,"E44.MirrorCS"),sQuery(id+"F0.wireOp",EDGE,"E6"),sQuery(id+"F0.wireOp",EDGE,"E45.MirrorCS"),sQuery(id+"F0.wireOp",EDGE,"E46.MirrorCS"),sQuery(id+"F0.wireOp",EDGE,"E47.MirrorCS"),sQuery(id+"F0.wireOp",EDGE,"E48.MirrorCS"),sQuery(id+"F0.wireOp",EDGE,"E49.MirrorCS"),sQuery(id+"F0.wireOp",EDGE,"E52.MirrorCS"),sQuery(id+"F0.wireOp",EDGE,"E53.MirrorCS"),sQuery(id+"F0.wireOp",EDGE,"E56.MirrorCS"),sQuery(id+"F0.wireOp",EDGE,"E57.MirrorCS"),sQuery(id+"F0.wireOp",EDGE,"E58.MirrorCS"),sQuery(id+"F0.wireOp",EDGE,"E60.MirrorCS"),sQuery(id+"F0.wireOp",EDGE,"E61.MirrorCS"),sQuery(id+"F0.wireOp",EDGE,"E63.MirrorCS"),sQuery(id+"F0.wireOp",EDGE,"E64.MirrorCS"),sQuery(id+"F0.wireOp",EDGE,"E65.MirrorCS"),sQuery(id+"F0.wireOp",EDGE,"E68.MirrorCS"),sQuery(id+"F0.wireOp",EDGE,"E70.MirrorCS"),sQuery(id+"F0.wireOp",EDGE,"E71.MirrorCS"),sQuery(id+"F0.wireOp",EDGE,"E73.MirrorCS"),sQuery(id+"F0.wireOp",EDGE,"E74.MirrorCS"),sQuery(id+"F0.wireOp",EDGE,"E76.MirrorCS"),sQuery(id+"F0.wireOp",EDGE,"E78.MirrorCS"),sQuery(id+"F0.wireOp",EDGE,"E79.MirrorCS"),sQuery(id+"F0.wireOp",EDGE,"E81.MirrorCS"),sQuery(id+"F0.wireOp",EDGE,"E82.MirrorCS"),sQuery(id+"F0.wireOp",EDGE,"E84.MirrorCS"),sQuery(id+"F0.wireOp",EDGE,"E85.MirrorCS"),sQuery(id+"F0.wireOp",EDGE,"E87.MirrorCS"),sQuery(id+"F0.wireOp",EDGE,"E89.MirrorCS"),sQuery(id+"F0.wireOp",EDGE,"E90.MirrorCS"),sQuery(id+"F0.wireOp",EDGE,"E91.MirrorCS"),sQuery(id+"F0.wireOp",EDGE,"E93.MirrorCS"),sQuery(id+"F0.wireOp",EDGE,"E95.MirrorCS"),sQuery(id+"F0.wireOp",EDGE,"E97.MirrorCS"),sQuery(id+"F0.wireOp",EDGE,"E98.MirrorCS"),sQuery(id+"F0.wireOp",EDGE,"E99.MirrorCS"),sQuery(id+"F0.wireOp",EDGE,"E8.9.1"),sQuery(id+"F0.wireOp",EDGE,"E103.MirrorCS"),sQuery(id+"F0.wireOp",EDGE,"E104.MirrorCS"),sQuery(id+"F0.wireOp",EDGE,"E105.MirrorCS"),sQuery(id+"F0.wireOp",EDGE,"E107.MirrorCS"),sQuery(id+"F0.wireOp",EDGE,"E108.MirrorCS"),sQuery(id+"F0.wireOp",EDGE,"E110.MirrorCS"),sQuery(id+"F0.wireOp",EDGE,"E114"),sQuery(id+"F0.wireOp",EDGE,"E115"),sQuery(id+"F0.wireOp",EDGE,"E116"),sQuery(id+"F0.wireOp",EDGE,"E121.bottom"),sQuery(id+"F0.wireOp",EDGE,"E121.top"),sQuery(id+"F0.wireOp",EDGE,"E122.left"),sQuery(id+"F0.wireOp",EDGE,"E122.right")])],"isStart":false});
            var Q1;
            Q1=makeQuery(id+"F1.opExtrude","CAP_FACE",FACE,{"disambiguationData":[OSD([sQuery(id+"F0.wireOp",EDGE,"E0"),sQuery(id+"F0.wireOp",EDGE,"E7.1.0"),sQuery(id+"F0.wireOp",EDGE,"E7.1.1"),sQuery(id+"F0.wireOp",EDGE,"E7.1.2"),sQuery(id+"F0.wireOp",EDGE,"E7.1.3"),sQuery(id+"F0.wireOp",EDGE,"E7.2.0"),sQuery(id+"F0.wireOp",EDGE,"E7.2.1"),sQuery(id+"F0.wireOp",EDGE,"E7.2.2"),sQuery(id+"F0.wireOp",EDGE,"E7.2.3"),sQuery(id+"F0.wireOp",EDGE,"E7.3.0"),sQuery(id+"F0.wireOp",EDGE,"E7.3.1"),sQuery(id+"F0.wireOp",EDGE,"E7.3.2"),sQuery(id+"F0.wireOp",EDGE,"E7.3.3"),sQuery(id+"F0.wireOp",EDGE,"E7.4.0"),sQuery(id+"F0.wireOp",EDGE,"E7.4.1"),sQuery(id+"F0.wireOp",EDGE,"E7.4.2"),sQuery(id+"F0.wireOp",EDGE,"E7.4.3"),sQuery(id+"F0.wireOp",EDGE,"E7.5.0"),sQuery(id+"F0.wireOp",EDGE,"E7.5.1"),sQuery(id+"F0.wireOp",EDGE,"E7.5.2"),sQuery(id+"F0.wireOp",EDGE,"E7.5.3"),sQuery(id+"F0.wireOp",EDGE,"E7.6.0"),sQuery(id+"F0.wireOp",EDGE,"E7.6.1"),sQuery(id+"F0.wireOp",EDGE,"E7.6.2"),sQuery(id+"F0.wireOp",EDGE,"E7.6.3"),sQuery(id+"F0.wireOp",EDGE,"E7.7.0"),sQuery(id+"F0.wireOp",EDGE,"E7.7.1"),sQuery(id+"F0.wireOp",EDGE,"E7.7.2"),sQuery(id+"F0.wireOp",EDGE,"E7.7.3"),sQuery(id+"F0.wireOp",EDGE,"E7.8.0"),sQuery(id+"F0.wireOp",EDGE,"E7.8.1"),sQuery(id+"F0.wireOp",EDGE,"E7.8.2"),sQuery(id+"F0.wireOp",EDGE,"E7.8.3"),sQuery(id+"F0.wireOp",EDGE,"E7.9.0"),sQuery(id+"F0.wireOp",EDGE,"E7.9.1"),sQuery(id+"F0.wireOp",EDGE,"E7.9.2"),sQuery(id+"F0.wireOp",EDGE,"E7.9.3"),sQuery(id+"F0.wireOp",EDGE,"E8.1.1"),sQuery(id+"F0.wireOp",EDGE,"E8.1.2"),sQuery(id+"F0.wireOp",EDGE,"E8.1.3"),sQuery(id+"F0.wireOp",EDGE,"E8.1.4"),sQuery(id+"F0.wireOp",EDGE,"E8.2.1"),sQuery(id+"F0.wireOp",EDGE,"E8.2.2"),sQuery(id+"F0.wireOp",EDGE,"E8.2.3"),sQuery(id+"F0.wireOp",EDGE,"E8.2.4"),sQuery(id+"F0.wireOp",EDGE,"E8.3.1"),sQuery(id+"F0.wireOp",EDGE,"E8.3.2"),sQuery(id+"F0.wireOp",EDGE,"E8.3.3"),sQuery(id+"F0.wireOp",EDGE,"E8.3.4"),sQuery(id+"F0.wireOp",EDGE,"E8.4.1"),sQuery(id+"F0.wireOp",EDGE,"E8.4.2"),sQuery(id+"F0.wireOp",EDGE,"E8.4.3"),sQuery(id+"F0.wireOp",EDGE,"E8.4.4"),sQuery(id+"F0.wireOp",EDGE,"E8.5.1"),sQuery(id+"F0.wireOp",EDGE,"E8.5.2"),sQuery(id+"F0.wireOp",EDGE,"E8.5.3"),sQuery(id+"F0.wireOp",EDGE,"E8.5.4"),sQuery(id+"F0.wireOp",EDGE,"E8.6.1"),sQuery(id+"F0.wireOp",EDGE,"E8.6.2"),sQuery(id+"F0.wireOp",EDGE,"E8.6.3"),sQuery(id+"F0.wireOp",EDGE,"E8.6.4"),sQuery(id+"F0.wireOp",EDGE,"E8.7.1"),sQuery(id+"F0.wireOp",EDGE,"E8.7.2"),sQuery(id+"F0.wireOp",EDGE,"E8.7.3"),sQuery(id+"F0.wireOp",EDGE,"E8.7.4"),sQuery(id+"F0.wireOp",EDGE,"E8.8.1"),sQuery(id+"F0.wireOp",EDGE,"E8.8.2"),sQuery(id+"F0.wireOp",EDGE,"E8.8.3"),sQuery(id+"F0.wireOp",EDGE,"E8.8.4"),sQuery(id+"F0.wireOp",EDGE,"E9.MirrorCS"),sQuery(id+"F0.wireOp",EDGE,"E10.MirrorCS"),sQuery(id+"F0.wireOp",EDGE,"E13.MirrorCS"),sQuery(id+"F0.wireOp",EDGE,"E14.MirrorCS"),sQuery(id+"F0.wireOp",EDGE,"E15.MirrorCS"),sQuery(id+"F0.wireOp",EDGE,"E5"),sQuery(id+"F0.wireOp",EDGE,"E3"),sQuery(id+"F0.wireOp",EDGE,"E4"),sQuery(id+"F0.wireOp",EDGE,"E16.MirrorCS"),sQuery(id+"F0.wireOp",EDGE,"E18.MirrorCS"),sQuery(id+"F0.wireOp",EDGE,"E19.MirrorCS"),sQuery(id+"F0.wireOp",EDGE,"E20.MirrorCS"),sQuery(id+"F0.wireOp",EDGE,"E21.MirrorCS"),sQuery(id+"F0.wireOp",EDGE,"E23.MirrorCS"),sQuery(id+"F0.wireOp",EDGE,"E24.MirrorCS"),sQuery(id+"F0.wireOp",EDGE,"E25.MirrorCS"),sQuery(id+"F0.wireOp",EDGE,"E8.9.2"),sQuery(id+"F0.wireOp",EDGE,"E26.MirrorCS"),sQuery(id+"F0.wireOp",EDGE,"E27.MirrorCS"),sQuery(id+"F0.wireOp",EDGE,"E28.MirrorCS"),sQuery(id+"F0.wireOp",EDGE,"E29.MirrorCS"),sQuery(id+"F0.wireOp",EDGE,"E31.MirrorCS"),sQuery(id+"F0.wireOp",EDGE,"E8.9.3"),sQuery(id+"F0.wireOp",EDGE,"E32.MirrorCS"),sQuery(id+"F0.wireOp",EDGE,"E33.MirrorCS"),sQuery(id+"F0.wireOp",EDGE,"E34.MirrorCS"),sQuery(id+"F0.wireOp",EDGE,"E37.MirrorCS"),sQuery(id+"F0.wireOp",EDGE,"E39.MirrorCS"),sQuery(id+"F0.wireOp",EDGE,"E41.MirrorCS"),sQuery(id+"F0.wireOp",EDGE,"E42.MirrorCS"),sQuery(id+"F0.wireOp",EDGE,"E8.9.4"),sQuery(id+"F0.wireOp",EDGE,"E44.MirrorCS"),sQuery(id+"F0.wireOp",EDGE,"E6"),sQuery(id+"F0.wireOp",EDGE,"E45.MirrorCS"),sQuery(id+"F0.wireOp",EDGE,"E46.MirrorCS"),sQuery(id+"F0.wireOp",EDGE,"E47.MirrorCS"),sQuery(id+"F0.wireOp",EDGE,"E48.MirrorCS"),sQuery(id+"F0.wireOp",EDGE,"E49.MirrorCS"),sQuery(id+"F0.wireOp",EDGE,"E52.MirrorCS"),sQuery(id+"F0.wireOp",EDGE,"E53.MirrorCS"),sQuery(id+"F0.wireOp",EDGE,"E56.MirrorCS"),sQuery(id+"F0.wireOp",EDGE,"E57.MirrorCS"),sQuery(id+"F0.wireOp",EDGE,"E58.MirrorCS"),sQuery(id+"F0.wireOp",EDGE,"E60.MirrorCS"),sQuery(id+"F0.wireOp",EDGE,"E61.MirrorCS"),sQuery(id+"F0.wireOp",EDGE,"E63.MirrorCS"),sQuery(id+"F0.wireOp",EDGE,"E64.MirrorCS"),sQuery(id+"F0.wireOp",EDGE,"E65.MirrorCS"),sQuery(id+"F0.wireOp",EDGE,"E68.MirrorCS"),sQuery(id+"F0.wireOp",EDGE,"E70.MirrorCS"),sQuery(id+"F0.wireOp",EDGE,"E71.MirrorCS"),sQuery(id+"F0.wireOp",EDGE,"E73.MirrorCS"),sQuery(id+"F0.wireOp",EDGE,"E74.MirrorCS"),sQuery(id+"F0.wireOp",EDGE,"E76.MirrorCS"),sQuery(id+"F0.wireOp",EDGE,"E78.MirrorCS"),sQuery(id+"F0.wireOp",EDGE,"E79.MirrorCS"),sQuery(id+"F0.wireOp",EDGE,"E81.MirrorCS"),sQuery(id+"F0.wireOp",EDGE,"E82.MirrorCS"),sQuery(id+"F0.wireOp",EDGE,"E84.MirrorCS"),sQuery(id+"F0.wireOp",EDGE,"E85.MirrorCS"),sQuery(id+"F0.wireOp",EDGE,"E87.MirrorCS"),sQuery(id+"F0.wireOp",EDGE,"E89.MirrorCS"),sQuery(id+"F0.wireOp",EDGE,"E90.MirrorCS"),sQuery(id+"F0.wireOp",EDGE,"E91.MirrorCS"),sQuery(id+"F0.wireOp",EDGE,"E93.MirrorCS"),sQuery(id+"F0.wireOp",EDGE,"E95.MirrorCS"),sQuery(id+"F0.wireOp",EDGE,"E97.MirrorCS"),sQuery(id+"F0.wireOp",EDGE,"E98.MirrorCS"),sQuery(id+"F0.wireOp",EDGE,"E99.MirrorCS"),sQuery(id+"F0.wireOp",EDGE,"E8.9.1"),sQuery(id+"F0.wireOp",EDGE,"E103.MirrorCS"),sQuery(id+"F0.wireOp",EDGE,"E104.MirrorCS"),sQuery(id+"F0.wireOp",EDGE,"E105.MirrorCS"),sQuery(id+"F0.wireOp",EDGE,"E107.MirrorCS"),sQuery(id+"F0.wireOp",EDGE,"E108.MirrorCS"),sQuery(id+"F0.wireOp",EDGE,"E110.MirrorCS"),sQuery(id+"F0.wireOp",EDGE,"E114"),sQuery(id+"F0.wireOp",EDGE,"E115"),sQuery(id+"F0.wireOp",EDGE,"E116"),sQuery(id+"F0.wireOp",EDGE,"E121.bottom"),sQuery(id+"F0.wireOp",EDGE,"E121.top"),sQuery(id+"F0.wireOp",EDGE,"E122.left"),sQuery(id+"F0.wireOp",EDGE,"E122.right")])],"isStart":false});
            var sketch = newSketch(context, id + "F2", { "sketchPlane" : qUnion([Q0, Q1])});
            skLineSegment(sketch, "E127", {"start": v(0, 0) * mm, "end": v(0, 9.53) * mm});
            skLineSegment(sketch, "E128", {"start": v(0, 0) * mm, "end": v(0, -9.53) * mm});
            skCircle(sketch, "E129", {"center": v(0, 9.53) * mm, "radius": 1.27 * mm});
            skCircle(sketch, "E130", {"center": v(0, -9.53) * mm, "radius": 1.27 * mm});
            skSolve(sketch);
        }
        {
            var Q0;
            Q0 = qSketchRegion(id + "F2", true);
            extrude(context, id + "F3", {"entities" : qUnion([Q0]), "operationType" : NewBodyOperationType.ADD, "depth" : 6.35 * mm});
        }
    });
